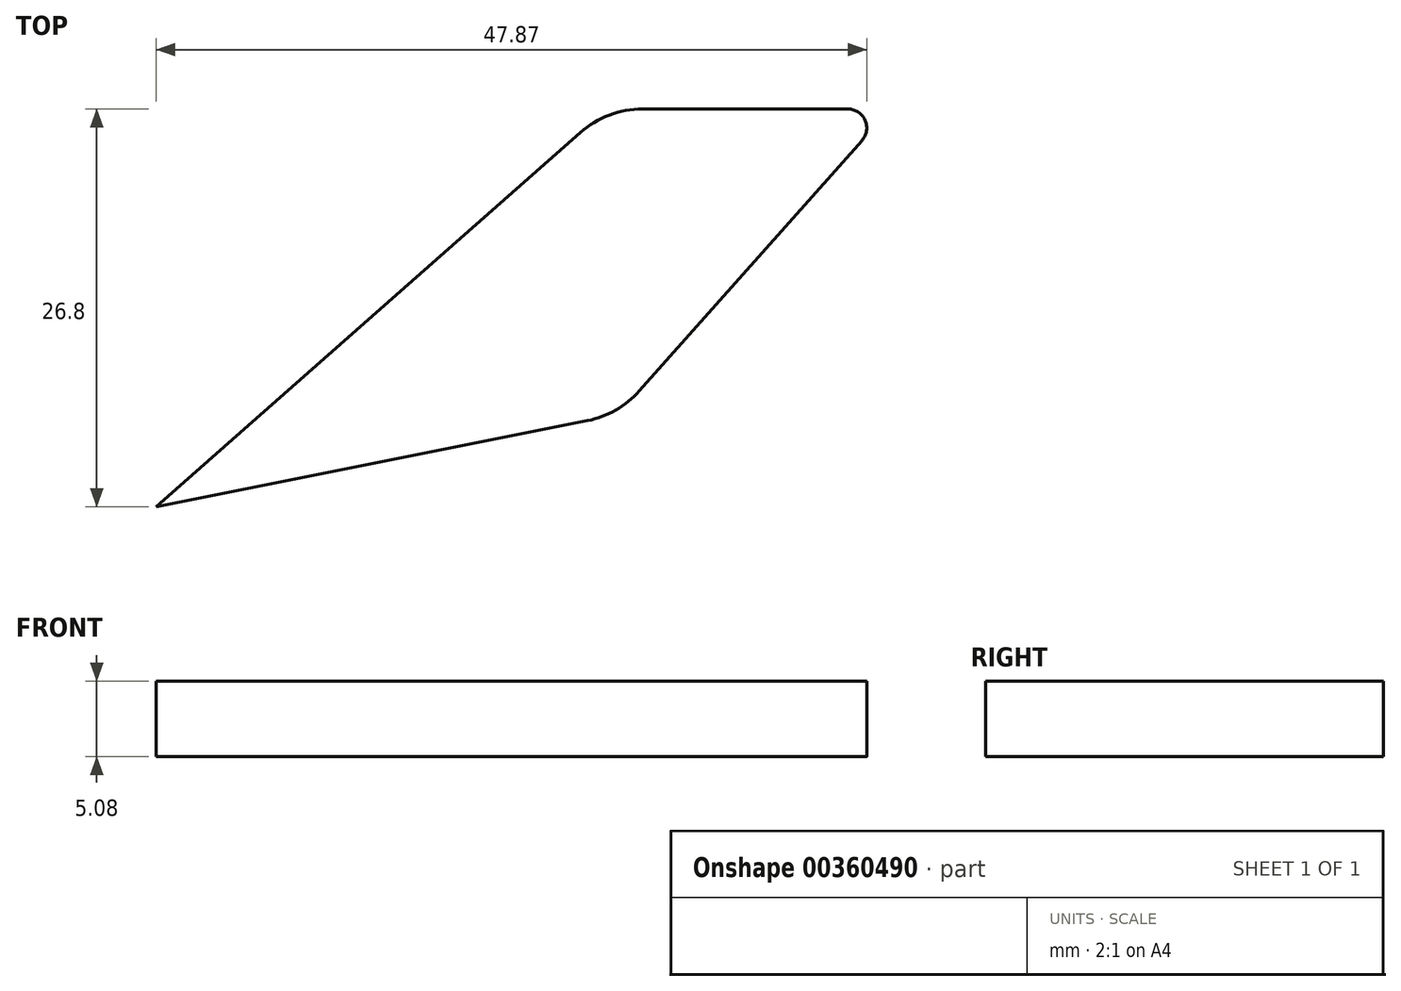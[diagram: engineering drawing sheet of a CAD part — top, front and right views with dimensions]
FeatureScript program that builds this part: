
annotation { "Feature Type Name" : "Feature", "Feature Type Description" : "" }
export const myFeature = defineFeature(function(context is Context, id is Id, definition is map)
    precondition{}
    {
        {
            var Q0;
            Q0=qCreatedBy(makeId("Top.planeOp"),FACE);
            var sketch = newSketch(context, id + "F0", { "sketchPlane" : qUnion([Q0])});
            skLineSegment(sketch, "E0", {"start": v(-59.19, 9.3) * mm, "end": v(-30.62, 34.5) * mm});
            skLineSegment(sketch, "E1", {"start": v(-26.42, 36.09) * mm, "end": v(-12.6, 36.09) * mm});
            skLineSegment(sketch, "E2", {"start": v(-11.64, 33.97) * mm, "end": v(-26.64, 17.1) * mm});
            skLineSegment(sketch, "E3", {"start": v(-30.14, 15.09) * mm, "end": v(-59.19, 9.3) * mm});
            skPoint(sketch, "E4.visualSharp", {"position": v(-28.82, 36.09) * mm});
            skArc(sketch, "E4.filletArc", {"start": v(-26.42, 36.09) * mm, "mid": v(-28.66, 35.67) * mm, "end": v(-30.62, 34.5) * mm});
            skPoint(sketch, "E5.visualSharp", {"position": v(-28.05, 15.5) * mm});
            skArc(sketch, "E5.filletArc", {"start": v(-30.14, 15.09) * mm, "mid": v(-28.23, 15.8) * mm, "end": v(-26.64, 17.1) * mm});
            skPoint(sketch, "E6.visualSharp", {"position": v(-9.77, 36.09) * mm});
            skArc(sketch, "E6.filletArc", {"start": v(-11.64, 33.97) * mm, "mid": v(-11.44, 35.34) * mm, "end": v(-12.6, 36.09) * mm});
            skSolve(sketch);
        }
        {
            var Q0;
            Q0=makeQuery(id+"F0.imprint","IMPRINT",FACE,{"disambiguationData":[TD([[makeQuery(id+"F0.imprint","IMPRINT",EDGE,{"derivedFrom":sQuery(id+"F0.wireOp",EDGE,"E0")}),-1.0]])]});
            extrude(context, id + "F1", {"entities" : qUnion([Q0]), "depth" : 5.08 * mm});
        }
    });
